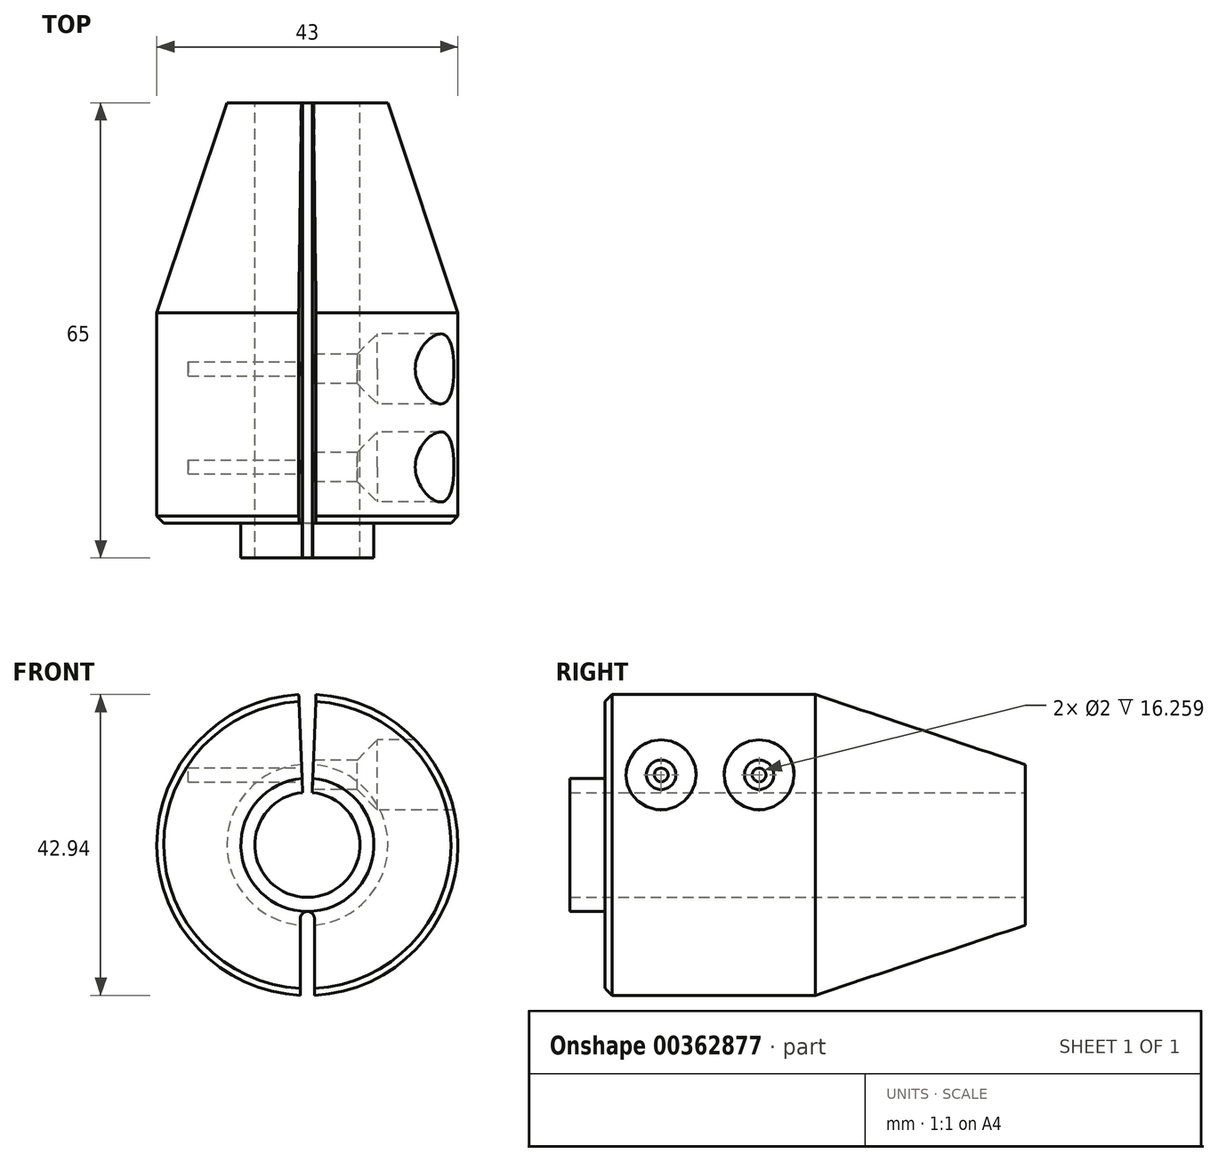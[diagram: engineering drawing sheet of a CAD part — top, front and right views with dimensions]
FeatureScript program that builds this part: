
annotation { "Feature Type Name" : "Feature", "Feature Type Description" : "" }
export const myFeature = defineFeature(function(context is Context, id is Id, definition is map)
    precondition{}
    {
        {
            var Q0;
            Q0=qCreatedBy(makeId("Front.planeOp"),FACE);
            var sketch = newSketch(context, id + "F0", { "sketchPlane" : qUnion([Q0])});
            skCircle(sketch, "E0", {"center": v(0, 0) * mm, "radius": 7.5 * mm});
            skCircle(sketch, "E1.0", {"center": v(0, 0) * mm, "radius": 9.5 * mm});
            skCircle(sketch, "E2", {"center": v(0, 0) * mm, "radius": 21.5 * mm});
            skSolve(sketch);
        }
        {
            var Q0;
            Q0=makeQuery(id+"F0.imprint","IMPRINT",FACE,{"disambiguationData":[TD([[makeQuery(id+"F0.imprint","IMPRINT",EDGE,{"derivedFrom":sQuery(id+"F0.wireOp",EDGE,"E0")}),-1.0]])]});
            extrude(context, id + "F1", {"entities" : qUnion([Q0]), "depth" : 5 * mm});
        }
        {
            var Q0;
            Q0=makeQuery(id+"F0.imprint","IMPRINT",FACE,{"disambiguationData":[TD([[makeQuery(id+"F0.imprint","IMPRINT",EDGE,{"derivedFrom":sQuery(id+"F0.wireOp",EDGE,"E1.0")}),-1.0]])]});
            var Q1;
            Q1=makeQuery(id+"F0.imprint","IMPRINT",FACE,{"disambiguationData":[TD([[makeQuery(id+"F0.imprint","IMPRINT",EDGE,{"derivedFrom":sQuery(id+"F0.wireOp",EDGE,"E0")}),-1.0]])]});
            extrude(context, id + "F2", {"entities" : qUnion([Q0, Q1]), "operationType" : NewBodyOperationType.ADD, "oppositeDirection" : true, "depth" : 60 * mm});
        }
        {
            var Q0;
            Q0=makeQuery(id+"F2.opExtrude","CAP_EDGE",EDGE,{"disambiguationData":[OSD([sQuery(id+"F0.wireOp",EDGE,"E2")])],"isStart":true});
            chamfer(context, id + "F3", {"entities" : qUnion([Q0]), "width" : 1 * mm, "tangentPropagation" : true});
        }
        {
            var Q0;
            Q0=makeQuery(id+"F2.opExtrude","CAP_EDGE",EDGE,{"disambiguationData":[OSD([sQuery(id+"F0.wireOp",EDGE,"E2")])],"isStart":false});
            chamfer(context, id + "F4", {"entities" : qUnion([Q0]), "chamferType" : ChamferType.TWO_OFFSETS, "width1" : 30 * mm, "oppositeDirection" : false, "width2" : 10 * mm, "tangentPropagation" : true});
        }
        {
            var Q0;
            Q0=qCreatedBy(makeId("Right.planeOp"),FACE);
            var sketch = newSketch(context, id + "F5", { "sketchPlane" : qUnion([Q0])});
            skLineSegment(sketch, "E3", {"start": v(0, 0) * mm, "end": v(30, 0) * mm, "construction": true});
            skLineSegment(sketch, "E4", {"start": v(30, 0) * mm, "end": v(30, 10) * mm, "construction": true});
            skLineSegment(sketch, "E5", {"start": v(30, 10) * mm, "end": v(0, 10) * mm, "construction": true});
            skLineSegment(sketch, "E6", {"start": v(0, 10) * mm, "end": v(0, 0) * mm, "construction": true});
            skLineSegment(sketch, "E7", {"start": v(0, 10) * mm, "end": v(8, 10) * mm, "construction": true});
            skLineSegment(sketch, "E8", {"start": v(30, 10) * mm, "end": v(22, 10) * mm, "construction": true});
            skCircle(sketch, "E9", {"center": v(8, 10) * mm, "radius": 1 * mm});
            skCircle(sketch, "E10", {"center": v(22, 10) * mm, "radius": 1 * mm});
            skCircle(sketch, "E11", {"center": v(8, 10) * mm, "radius": 2.1 * mm});
            skCircle(sketch, "E12", {"center": v(8, 10) * mm, "radius": 5 * mm});
            skCircle(sketch, "E13", {"center": v(22, 10) * mm, "radius": 2.1 * mm});
            skCircle(sketch, "E14", {"center": v(22, 10) * mm, "radius": 5 * mm});
            skSolve(sketch);
        }
        {
            var Q0;
            Q0=makeQuery(id+"F5.imprint","IMPRINT",FACE,{"disambiguationData":[TD([[makeQuery(id+"F5.imprint","IMPRINT",EDGE,{"derivedFrom":sQuery(id+"F5.wireOp",EDGE,"E9")}),1.0]])]});
            var Q1;
            Q1=makeQuery(id+"F5.imprint","IMPRINT",FACE,{"disambiguationData":[TD([[makeQuery(id+"F5.imprint","IMPRINT",EDGE,{"derivedFrom":sQuery(id+"F5.wireOp",EDGE,"E10")}),1.0]])]});
            extrude(context, id + "F6", {"entities" : qUnion([Q0, Q1]), "operationType" : NewBodyOperationType.REMOVE, "oppositeDirection" : true, "depth" : 17 * mm});
        }
        {
            var Q0;
            Q0=makeQuery(id+"F5.imprint","IMPRINT",FACE,{"disambiguationData":[TD([[makeQuery(id+"F5.imprint","IMPRINT",EDGE,{"derivedFrom":sQuery(id+"F5.wireOp",EDGE,"E9")}),-1.0]])]});
            var Q1;
            Q1=makeQuery(id+"F5.imprint","IMPRINT",FACE,{"disambiguationData":[TD([[makeQuery(id+"F5.imprint","IMPRINT",EDGE,{"derivedFrom":sQuery(id+"F5.wireOp",EDGE,"E9")}),1.0]])]});
            var Q2;
            Q2=makeQuery(id+"F5.imprint","IMPRINT",FACE,{"disambiguationData":[TD([[makeQuery(id+"F5.imprint","IMPRINT",EDGE,{"derivedFrom":sQuery(id+"F5.wireOp",EDGE,"E10")}),-1.0]])]});
            var Q3;
            Q3=makeQuery(id+"F5.imprint","IMPRINT",FACE,{"disambiguationData":[TD([[makeQuery(id+"F5.imprint","IMPRINT",EDGE,{"derivedFrom":sQuery(id+"F5.wireOp",EDGE,"E10")}),1.0]])]});
            extrude(context, id + "F7", {"entities" : qUnion([Q0, Q1, Q2, Q3]), "operationType" : NewBodyOperationType.REMOVE, "depth" : 25 * mm});
        }
        {
            var Q0;
            Q0=qCreatedBy(makeId("Right.planeOp"),FACE);
            cPlane(context, id + "F8", {"entities" : qUnion([Q0]), "cplaneType" : CPlaneType.OFFSET, "offset" : 6 * mm, "width" : 150 * mm, "height" : 150 * mm});
        }
        {
            var Q0;
            Q0=qCreatedBy(id+"F8.planeOp",FACE);
            var sketch = newSketch(context, id + "F9", { "sketchPlane" : qUnion([Q0])});
            skCircle(sketch, "E15.0", {"center": v(8, 10) * mm, "radius": 5 * mm});
            skCircle(sketch, "E16.0", {"center": v(22, 10) * mm, "radius": 5 * mm});
            skSolve(sketch);
        }
        {
            var Q0;
            Q0=makeQuery(id+"F9.imprint","IMPRINT",FACE,{"disambiguationData":[TD([[makeQuery(id+"F9.imprint","IMPRINT",EDGE,{"derivedFrom":sQuery(id+"F9.wireOp",EDGE,"E15.0")}),1.0]])]});
            var Q1;
            Q1=makeQuery(id+"F9.imprint","IMPRINT",FACE,{"disambiguationData":[TD([[makeQuery(id+"F9.imprint","IMPRINT",EDGE,{"derivedFrom":sQuery(id+"F9.wireOp",EDGE,"E16.0")}),1.0]])]});
            extrude(context, id + "F10", {"entities" : qUnion([Q0, Q1]), "operationType" : NewBodyOperationType.REMOVE, "depth" : 25 * mm});
        }
        {
            var Q0;
            Q0=makeQuery(id+"F10.boolean.opBoolean","COPY",EDGE,{"derivedFrom":makeQuery(id+"F10.opExtrude","CAP_EDGE",EDGE,{"disambiguationData":[OSD([sQuery(id+"F9.wireOp",EDGE,"E15.0")])],"isStart":true})});
            var Q1;
            Q1=makeQuery(id+"F10.boolean.opBoolean","COPY",EDGE,{"derivedFrom":makeQuery(id+"F10.opExtrude","CAP_EDGE",EDGE,{"disambiguationData":[OSD([sQuery(id+"F9.wireOp",EDGE,"E16.0")])],"isStart":true})});
            chamfer(context, id + "F11", {"entities" : qUnion([Q0, Q1]), "width" : 4 * mm, "tangentPropagation" : true});
        }
        {
            var Q0;
            Q0=qCreatedBy(makeId("Front.planeOp"),FACE);
            var sketch = newSketch(context, id + "F12", { "sketchPlane" : qUnion([Q0])});
            skCircle(sketch, "E17.0", {"center": v(0, 0) * mm, "radius": 9.5 * mm});
            skLineSegment(sketch, "E18", {"start": v(0, 0) * mm, "end": v(0, -9.5) * mm, "construction": true});
            skLineSegment(sketch, "E19", {"start": v(0, -9.5) * mm, "end": v(2, 40.46) * mm, "construction": true});
            skLineSegment(sketch, "E20", {"start": v(0, -9.5) * mm, "end": v(-2, 40.46) * mm, "construction": true});
            skLineSegment(sketch, "E21", {"start": v(0, 0) * mm, "end": v(0, 40.46) * mm, "construction": true});
            skLineSegment(sketch, "E22", {"start": v(0, 40.46) * mm, "end": v(2, 40.46) * mm, "construction": true});
            skLineSegment(sketch, "E23", {"start": v(0, 40.46) * mm, "end": v(-2, 40.46) * mm, "construction": true});
            skLineSegment(sketch, "E24", {"start": v(0, -9.5) * mm, "end": v(0, -24.5) * mm, "construction": true});
            skLineSegment(sketch, "E25", {"start": v(0, -9.5) * mm, "end": v(0, -10.5) * mm, "construction": true});
            skArc(sketch, "E26", {"start": v(1, -10.5) * mm, "mid": v(0, -9.5) * mm, "end": v(-1, -10.5) * mm});
            skLineSegment(sketch, "E27", {"start": v(-1, -10.5) * mm, "end": v(-1, -26.71) * mm});
            skLineSegment(sketch, "E28.MirrorCS", {"start": v(1, -10.5) * mm, "end": v(1, -26.71) * mm});
            skLineSegment(sketch, "E29", {"start": v(-1, -26.71) * mm, "end": v(1, -26.71) * mm});
            skLineSegment(sketch, "E30", {"start": v(0, 0) * mm, "end": v(0.38, 0.02) * mm});
            skLineSegment(sketch, "E31", {"start": v(0.38, 0.02) * mm, "end": v(-0.38, 0) * mm});
            skLineSegment(sketch, "E32", {"start": v(-0.38, 0) * mm, "end": v(-2, 40.46) * mm});
            skLineSegment(sketch, "E33", {"start": v(2, 40.46) * mm, "end": v(0.38, 0.02) * mm});
            skLineSegment(sketch, "E34", {"start": v(-2, 40.46) * mm, "end": v(2, 40.46) * mm});
            skSolve(sketch);
        }
        {
            var Q0;
            {var subQ5=sQuery(id+"F12.wireOp",EDGE,"E34");Q0=makeQuery(id+"F12.imprint","IMPRINT",FACE,{"disambiguationData":[TD([[makeQuery(id+"F12.imprint","IMPRINT",EDGE,{"derivedFrom":subQ5}),-1.0]])]});}
            var Q1;
            {var subQ5=sQuery(id+"F12.wireOp",EDGE,"E31");Q1=makeQuery(id+"F12.imprint","IMPRINT",FACE,{"disambiguationData":[TD([[makeQuery(id+"F12.imprint","IMPRINT",EDGE,{"derivedFrom":subQ5}),-1.0]])]});}
            var Q2;
            {var subQ1=sQuery(id+"F12.wireOp",EDGE,"E27");Q2=makeQuery(id+"F12.imprint","IMPRINT",FACE,{"disambiguationData":[TD([[makeQuery(id+"F12.imprint","IMPRINT",EDGE,{"derivedFrom":subQ1}),1.0]])]});}
            extrude(context, id + "F13", {"entities" : qUnion([Q0, Q1, Q2]), "operationType" : NewBodyOperationType.REMOVE, "endBound" : BoundingType.SYMMETRIC, "depth" : 140 * mm});
        }
    });
